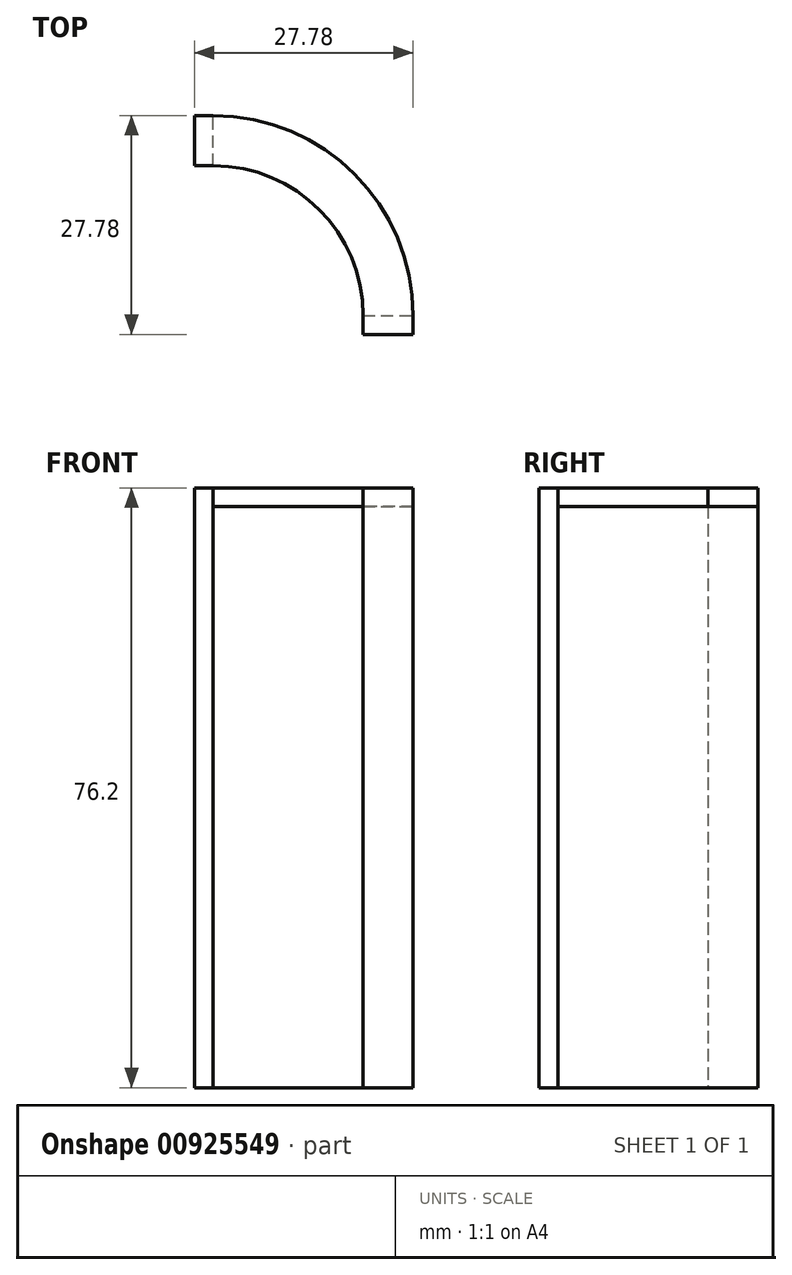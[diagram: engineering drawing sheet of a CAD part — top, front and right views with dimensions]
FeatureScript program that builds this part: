
annotation { "Feature Type Name" : "Feature", "Feature Type Description" : "" }
export const myFeature = defineFeature(function(context is Context, id is Id, definition is map)
    precondition{}
    {
        {
            var Q0;
            Q0=qCreatedBy(makeId("Top.planeOp"),FACE);
            var sketch = newSketch(context, id + "F0", { "sketchPlane" : qUnion([Q0])});
            skArc(sketch, "E0", {"start": v(19.05, 0) * mm, "mid": v(13.47, 13.47) * mm, "end": v(0, 19.05) * mm});
            skArc(sketch, "E1", {"start": v(25.4, 0) * mm, "mid": v(17.96, 17.96) * mm, "end": v(0, 25.4) * mm});
            skLineSegment(sketch, "E2", {"start": v(19.05, 0) * mm, "end": v(25.4, 0) * mm});
            skLineSegment(sketch, "E3", {"start": v(0, 19.05) * mm, "end": v(0, 25.4) * mm});
            skLineSegment(sketch, "E4.0", {"start": v(-2.38, 19.05) * mm, "end": v(-2.38, 25.4) * mm});
            skLineSegment(sketch, "E5", {"start": v(-2.38, 25.4) * mm, "end": v(0, 25.4) * mm});
            skLineSegment(sketch, "E6", {"start": v(-2.38, 19.05) * mm, "end": v(0, 19.05) * mm});
            skLineSegment(sketch, "E7.0", {"start": v(19.05, -2.38) * mm, "end": v(25.4, -2.38) * mm});
            skLineSegment(sketch, "E8", {"start": v(19.05, 0) * mm, "end": v(19.05, -2.38) * mm});
            skLineSegment(sketch, "E9", {"start": v(25.4, 0) * mm, "end": v(25.4, -2.38) * mm});
            skSolve(sketch);
        }
        {
            var Q0;
            {var subQ0=sQuery(id+"F0.wireOp",EDGE,"14636b3e-48a3-473e-8db5-16aa6e37203e.0");Q0=makeQuery(id+"F0.imprint","IMPRINT",FACE,{"disambiguationData":[TD([[makeQuery(id+"F0.imprint","IMPRINT",EDGE,{"derivedFrom":subQ0}),1.0]])]});}
            var Q1;
            {var subQ0=sQuery(id+"F0.wireOp",EDGE,"E2");Q1=makeQuery(id+"F0.imprint","IMPRINT",FACE,{"disambiguationData":[TD([[makeQuery(id+"F0.imprint","IMPRINT",EDGE,{"derivedFrom":subQ0}),1.0]])]});}
            var Q2;
            {var subQ0=sQuery(id+"F0.wireOp",EDGE,"E3");Q2=makeQuery(id+"F0.imprint","IMPRINT",FACE,{"disambiguationData":[TD([[makeQuery(id+"F0.imprint","IMPRINT",EDGE,{"derivedFrom":subQ0}),-1.0]])]});}
            extrude(context, id + "F1", {"entities" : qUnion([Q0, Q1, Q2]), "depth" : (3 / 16) / 50.8 * mm, "offsetDistance" : 30.48 * mm});
        }
        {
            var Q0;
            Q0=makeQuery(id+"F0.imprint","IMPRINT",FACE,{"disambiguationData":[TD([[makeQuery(id+"F0.imprint","IMPRINT",EDGE,{"derivedFrom":sQuery(id+"F0.wireOp",EDGE,"E2")}),-1.0]])]});
            var Q1;
            Q1=makeQuery(id+"F0.imprint","IMPRINT",FACE,{"disambiguationData":[TD([[makeQuery(id+"F0.imprint","IMPRINT",EDGE,{"derivedFrom":sQuery(id+"F0.wireOp",EDGE,"E3")}),1.0]])]});
            extrude(context, id + "F2", {"entities" : qUnion([Q0, Q1]), "operationType" : NewBodyOperationType.ADD, "depth" : 76.2 * mm, "offsetDistance" : 30.48 * mm});
        }
        {
            var Q0;
            Q0=makeQuery(id+"F2.opExtrude","CAP_FACE",FACE,{"disambiguationData":[OSD([sQuery(id+"F0.wireOp",EDGE,"E2"),sQuery(id+"F0.wireOp",EDGE,"E7.0"),sQuery(id+"F0.wireOp",EDGE,"E8"),sQuery(id+"F0.wireOp",EDGE,"E9")])],"isStart":false});
            var sketch = newSketch(context, id + "F3", { "sketchPlane" : qUnion([Q0])});
            skLineSegment(sketch, "E10.0.0", {"start": v(19.05, 0) * mm, "end": v(25.4, 0) * mm});
            skArc(sketch, "E10.0.1", {"start": v(25.4, 0) * mm, "mid": v(17.96, 17.96) * mm, "end": v(0, 25.4) * mm});
            skLineSegment(sketch, "E10.0.2", {"start": v(0, 25.4) * mm, "end": v(0, 19.05) * mm});
            skArc(sketch, "E10.0.3", {"start": v(0, 19.05) * mm, "mid": v(13.47, 13.47) * mm, "end": v(19.05, 0) * mm});
            skLineSegment(sketch, "E11.1.0", {"start": v(-2.38, 25.4) * mm, "end": v(-2.38, 19.05) * mm});
            skLineSegment(sketch, "E11.1.1", {"start": v(-2.38, 19.05) * mm, "end": v(0, 19.05) * mm});
            skLineSegment(sketch, "E11.1.2", {"start": v(0, 19.05) * mm, "end": v(0, 25.4) * mm});
            skLineSegment(sketch, "E11.1.3", {"start": v(0, 25.4) * mm, "end": v(-2.38, 25.4) * mm});
            skLineSegment(sketch, "E12.0", {"start": v(25.4, 0) * mm, "end": v(25.4, -2.38) * mm});
            skLineSegment(sketch, "E12.1", {"start": v(19.05, -2.38) * mm, "end": v(25.4, -2.38) * mm});
            skLineSegment(sketch, "E12.2", {"start": v(19.05, 0) * mm, "end": v(19.05, -2.38) * mm});
            skSolve(sketch);
        }
        {
            var Q0;
            Q0=makeQuery(id+"F3.imprint","IMPRINT",FACE,{"disambiguationData":[TD([[makeQuery(id+"F3.imprint","IMPRINT",EDGE,{"derivedFrom":sQuery(id+"F3.wireOp",EDGE,"E10.0.0")}),-1.0]])]});
            var Q1;
            Q1=makeQuery(id+"F3.imprint","IMPRINT",FACE,{"disambiguationData":[TD([[makeQuery(id+"F3.imprint","IMPRINT",EDGE,{"derivedFrom":sQuery(id+"F3.wireOp",EDGE,"E10.0.0")}),1.0]])]});
            var Q2;
            Q2=makeQuery(id+"F3.imprint","IMPRINT",FACE,{"disambiguationData":[TD([[makeQuery(id+"F3.imprint","IMPRINT",EDGE,{"derivedFrom":sQuery(id+"F3.wireOp",EDGE,"E11.1.0")}),1.0]])]});
            extrude(context, id + "F4", {"entities" : qUnion([Q0, Q1, Q2]), "operationType" : NewBodyOperationType.ADD, "depth" : 3 / 16 / 50.8 * mm, "offsetDistance" : 30.48 * mm});
        }
        {
            var Q0;
            Q0=makeQuery(id+"F1.opExtrude","CAP_FACE",FACE,{"disambiguationData":[OSD([sQuery(id+"F0.wireOp",EDGE,"E0"),sQuery(id+"F0.wireOp",EDGE,"E1"),sQuery(id+"F0.wireOp",EDGE,"E2"),sQuery(id+"F0.wireOp",EDGE,"E3")])],"isStart":false});
            extrude(context, id + "F5", {"entities" : qUnion([Q0]), "depth" : 73.82 * mm, "offsetDistance" : 30.48 * mm});
        }
    });
